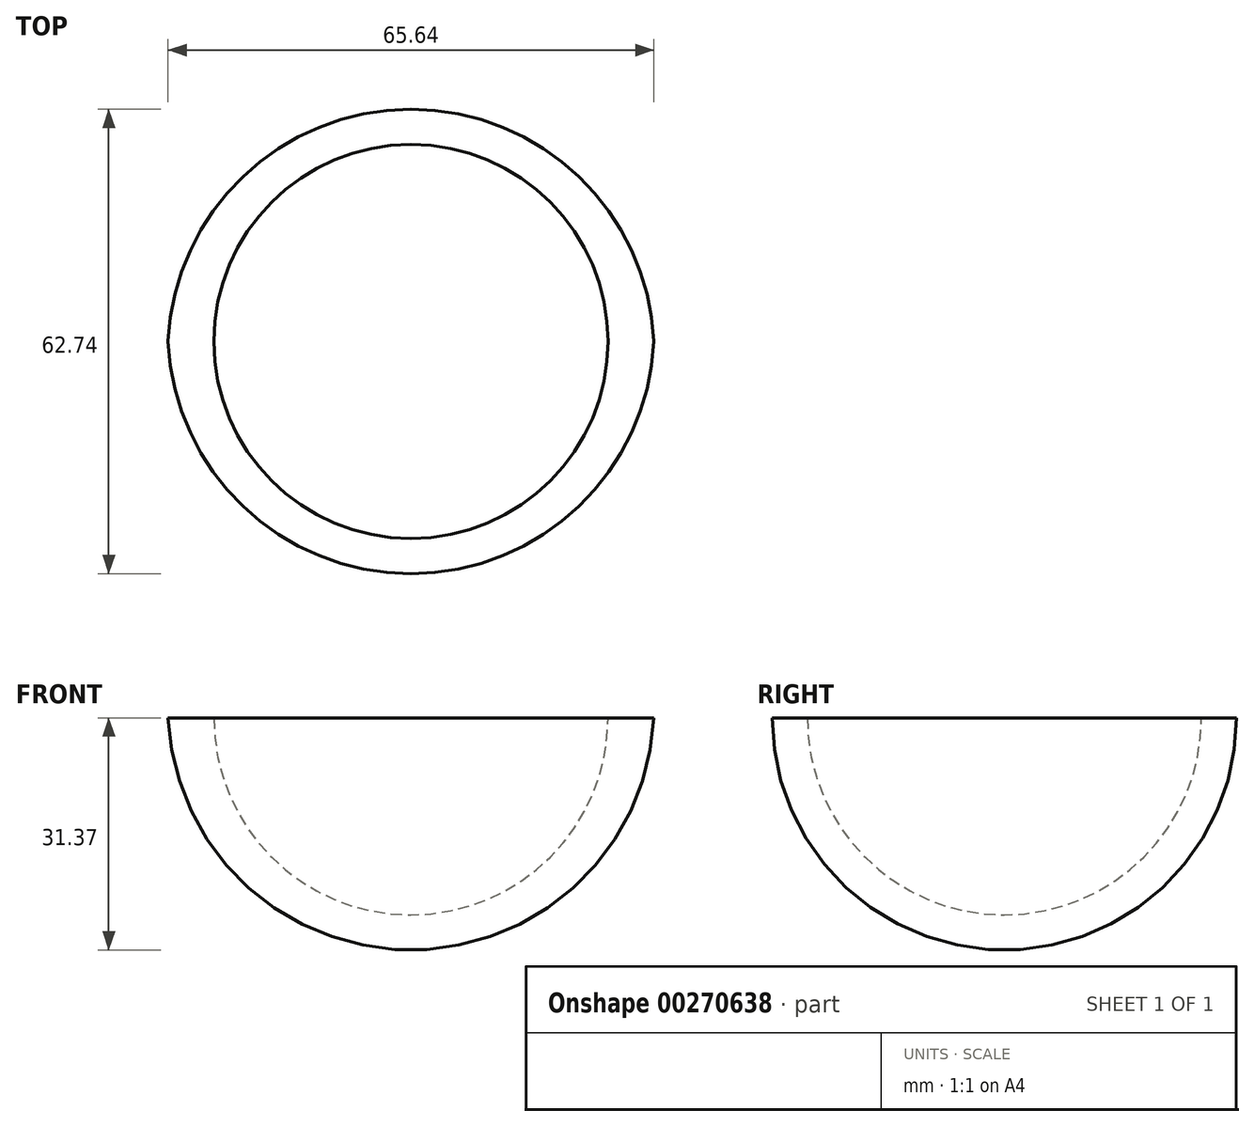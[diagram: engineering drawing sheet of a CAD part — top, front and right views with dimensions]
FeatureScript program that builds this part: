
annotation { "Feature Type Name" : "Feature", "Feature Type Description" : "" }
export const myFeature = defineFeature(function(context is Context, id is Id, definition is map)
    precondition{}
    {
        {
            var Q0;
            Q0=qCreatedBy(makeId("Top.planeOp"),FACE);
            var sketch = newSketch(context, id + "F0", { "sketchPlane" : qUnion([Q0])});
            skArc(sketch, "E0", {"start": v(32.82, 0) * mm, "mid": v(0, 31.37) * mm, "end": v(-32.82, 0) * mm});
            skLineSegment(sketch, "E1", {"start": v(-32.82, 0) * mm, "end": v(32.82, 0) * mm});
            skCircle(sketch, "E2", {"center": v(0, 0) * mm, "radius": 26.63 * mm});
            skSolve(sketch);
        }
        {
            var Q0;
            Q0=makeQuery(id+"F0.imprint","IMPRINT",FACE,{"disambiguationData":[TD([[makeQuery(id+"F0.imprint","IMPRINT",EDGE,{"derivedFrom":sQuery(id+"F0.wireOp",EDGE,"E0")}),1.0]])]});
            var Q1;
            Q1=sQuery(id+"F0.wireOp",EDGE,"E1");
            revolve(context, id + "F1", {"entities" : qUnion([Q0]), "axis" : qUnion([Q1]), "revolveType" : RevolveType.ONE_DIRECTION, "oppositeDirection" : true, "angle" : 180 * degree});
        }
        {
            var Q0;
            Q0 = qSketchRegion(id + "F0", true);
            extrude(context, id + "F2", {"entities" : qUnion([Q0]), "operationType" : NewBodyOperationType.REMOVE, "depth" : 2.54 * mm});
        }
    });
